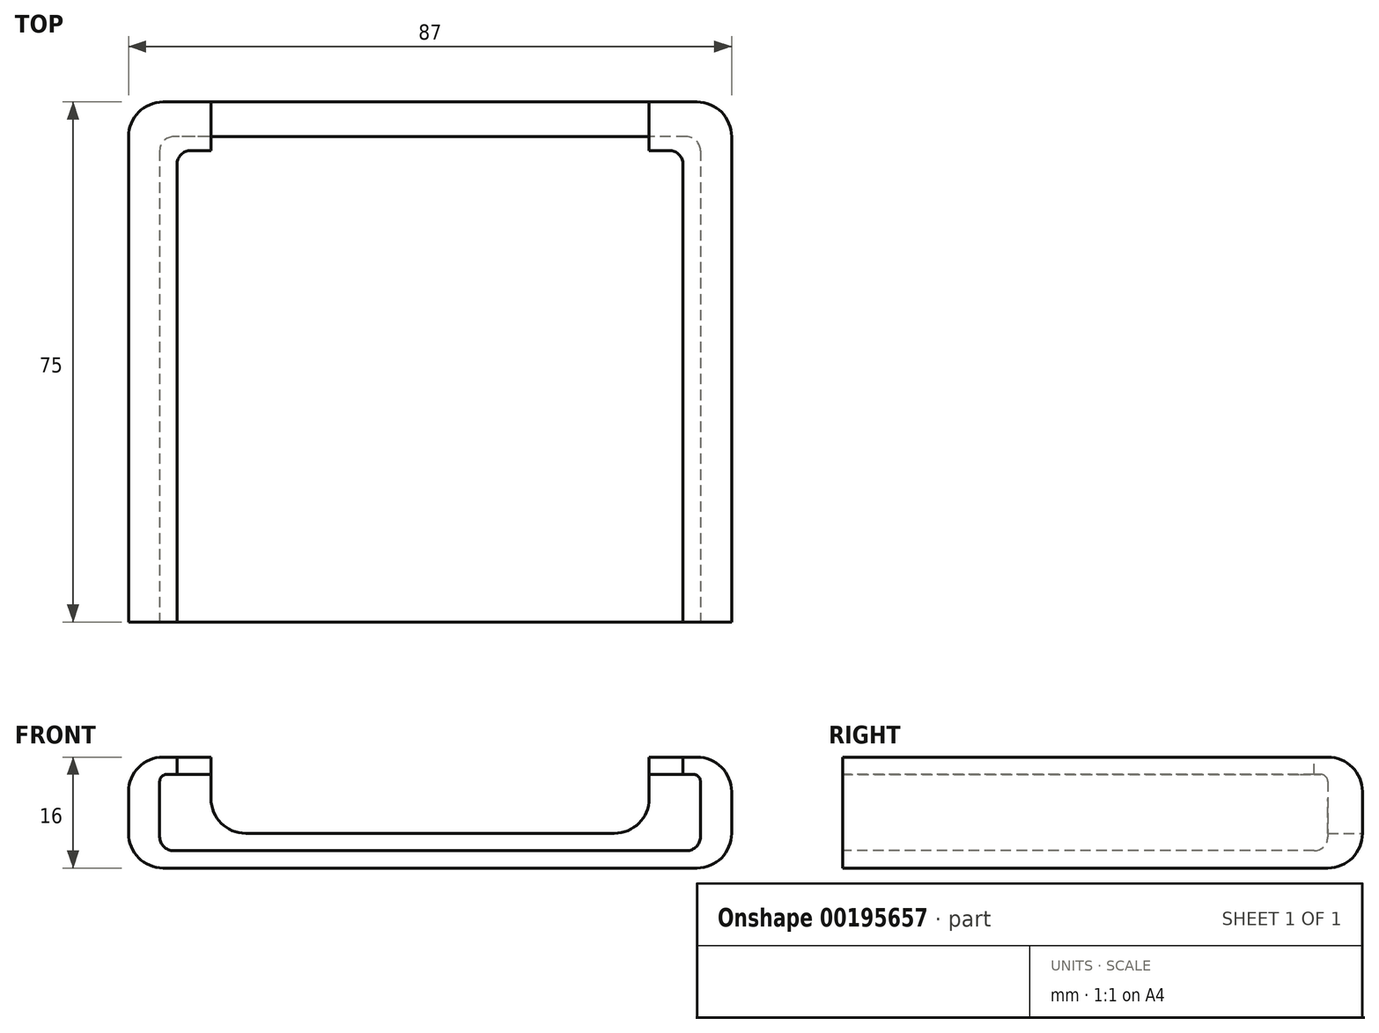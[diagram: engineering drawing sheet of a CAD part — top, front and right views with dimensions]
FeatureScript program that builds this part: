
annotation { "Feature Type Name" : "Feature", "Feature Type Description" : "" }
export const myFeature = defineFeature(function(context is Context, id is Id, definition is map)
    precondition{}
    {
        {
            var Q0;
            Q0=qCreatedBy(makeId("Front.planeOp"),FACE);
            var sketch = newSketch(context, id + "F0", { "sketchPlane" : qUnion([Q0])});
            skLineSegment(sketch, "E0.bottom", {"start": v(43.5, 8) * mm, "end": v(-43.5, 8) * mm});
            skLineSegment(sketch, "E0.top", {"start": v(43.5, -8) * mm, "end": v(-43.5, -8) * mm});
            skLineSegment(sketch, "E0.left", {"start": v(43.5, 8) * mm, "end": v(43.5, -8) * mm});
            skLineSegment(sketch, "E0.right", {"start": v(-43.5, 8) * mm, "end": v(-43.5, -8) * mm});
            skPoint(sketch, "E0.middle", {"position": v(0, 0) * mm});
            skSolve(sketch);
        }
        {
            var Q0;
            Q0=makeQuery(id+"F0.imprint","IMPRINT",FACE,{"disambiguationData":[TD([[makeQuery(id+"F0.imprint","IMPRINT",EDGE,{"derivedFrom":sQuery(id+"F0.wireOp",EDGE,"E0.bottom")}),1.0]])]});
            extrude(context, id + "F1", {"entities" : qUnion([Q0]), "depth" : 75 * mm});
        }
        {
            var Q0;
            Q0=makeQuery(id+"F1.opExtrude","SWEPT_EDGE",EDGE,{"disambiguationData":[OSD([sQuery(id+"F0.wireOp",EDGE,"E0.bottom"),sQuery(id+"F0.wireOp",EDGE,"E0.right")])]});
            var Q1;
            Q1=makeQuery(id+"F1.opExtrude","SWEPT_EDGE",EDGE,{"disambiguationData":[OSD([sQuery(id+"F0.wireOp",EDGE,"E0.bottom"),sQuery(id+"F0.wireOp",EDGE,"E0.left")])]});
            var Q2;
            Q2=makeQuery(id+"F1.opExtrude","SWEPT_EDGE",EDGE,{"disambiguationData":[OSD([sQuery(id+"F0.wireOp",EDGE,"E0.top"),sQuery(id+"F0.wireOp",EDGE,"E0.left")])]});
            var Q3;
            Q3=makeQuery(id+"F1.opExtrude","SWEPT_EDGE",EDGE,{"disambiguationData":[OSD([sQuery(id+"F0.wireOp",EDGE,"E0.top"),sQuery(id+"F0.wireOp",EDGE,"E0.right")])]});
            var Q4;
            Q4=makeQuery(id+"F1.opExtrude","CAP_EDGE",EDGE,{"disambiguationData":[OSD([sQuery(id+"F0.wireOp",EDGE,"E0.bottom")])],"isStart":true});
            var Q5;
            Q5=makeQuery(id+"F1.opExtrude","CAP_EDGE",EDGE,{"disambiguationData":[OSD([sQuery(id+"F0.wireOp",EDGE,"E0.top")])],"isStart":true});
            var Q6;
            Q6=makeQuery(id+"F1.opExtrude","CAP_EDGE",EDGE,{"disambiguationData":[OSD([sQuery(id+"F0.wireOp",EDGE,"E0.right")])],"isStart":true});
            var Q7;
            Q7=makeQuery(id+"F1.opExtrude","CAP_EDGE",EDGE,{"disambiguationData":[OSD([sQuery(id+"F0.wireOp",EDGE,"E0.left")])],"isStart":true});
            fillet(context, id + "F2", {"entities" : qUnion([Q0, Q1, Q2, Q3, Q4, Q5, Q6, Q7]), "radius" : 5 * mm, "tangentPropagation" : true, "allowEdgeOverflow" : false});
        }
        {
            var Q0;
            Q0=makeQuery(id+"F1.opExtrude","CAP_FACE",FACE,{"disambiguationData":[OSD([sQuery(id+"F0.wireOp",EDGE,"E0.bottom"),sQuery(id+"F0.wireOp",EDGE,"E0.top"),sQuery(id+"F0.wireOp",EDGE,"E0.left"),sQuery(id+"F0.wireOp",EDGE,"E0.right")])],"isStart":false});
            var sketch = newSketch(context, id + "F3", { "sketchPlane" : qUnion([Q0])});
            skLineSegment(sketch, "E1.bottom", {"start": v(39, 5.5) * mm, "end": v(-39, 5.5) * mm});
            skLineSegment(sketch, "E1.top", {"start": v(39, -5.5) * mm, "end": v(-39, -5.5) * mm});
            skLineSegment(sketch, "E1.left", {"start": v(39, 5.5) * mm, "end": v(39, -5.5) * mm});
            skLineSegment(sketch, "E1.right", {"start": v(-39, 5.5) * mm, "end": v(-39, -5.5) * mm});
            skPoint(sketch, "E1.middle", {"position": v(0, 0) * mm});
            skSolve(sketch);
        }
        {
            var Q0;
            Q0 = qSketchRegion(id + "F3", true);
            extrude(context, id + "F4", {"entities" : qUnion([Q0]), "operationType" : NewBodyOperationType.REMOVE, "oppositeDirection" : true, "depth" : 70 * mm});
        }
        {
            var Q0;
            Q0=makeQuery(id+"F1.opExtrude","SWEPT_FACE",FACE,{"disambiguationData":[OSD([sQuery(id+"F0.wireOp",EDGE,"E0.bottom")])]});
            var sketch = newSketch(context, id + "F5", { "sketchPlane" : qUnion([Q0])});
            skLineSegment(sketch, "E2.bottom", {"start": v(36.5, -7) * mm, "end": v(-36.5, -7) * mm});
            skLineSegment(sketch, "E2.top", {"start": v(36.5, -143) * mm, "end": v(-36.5, -143) * mm});
            skLineSegment(sketch, "E2.left", {"start": v(36.5, -7) * mm, "end": v(36.5, -143) * mm});
            skLineSegment(sketch, "E2.right", {"start": v(-36.5, -7) * mm, "end": v(-36.5, -143) * mm});
            skPoint(sketch, "E2.middle", {"position": v(0, -75) * mm});
            skSolve(sketch);
        }
        {
            var Q0;
            {var subQ0=sQuery(id+"F5.wireOp",EDGE,"E2.bottom");Q0=makeQuery(id+"F5.imprint","IMPRINT",FACE,{"disambiguationData":[TD([[makeQuery(id+"F5.imprint","IMPRINT",EDGE,{"derivedFrom":subQ0}),1.0]])]});}
            extrude(context, id + "F6", {"entities" : qUnion([Q0]), "operationType" : NewBodyOperationType.REMOVE, "endBound" : BoundingType.UP_TO_NEXT, "oppositeDirection" : true, "depth" : 25 * mm});
        }
        {
            var Q0;
            Q0=makeQuery(id+"F6.boolean.opBoolean","COPY",EDGE,{"derivedFrom":makeQuery(id+"F6.opExtrude","SWEPT_EDGE",EDGE,{"disambiguationData":[OSD([sQuery(id+"F5.wireOp",EDGE,"E2.bottom"),sQuery(id+"F5.wireOp",EDGE,"E2.left")])]})});
            var Q1;
            Q1=makeQuery(id+"F6.boolean.opBoolean","COPY",EDGE,{"derivedFrom":makeQuery(id+"F6.opExtrude","SWEPT_EDGE",EDGE,{"disambiguationData":[OSD([sQuery(id+"F5.wireOp",EDGE,"E2.bottom"),sQuery(id+"F5.wireOp",EDGE,"E2.right")])]})});
            var Q2;
            Q2=makeQuery(id+"F4.boolean.opBoolean","COPY",EDGE,{"derivedFrom":makeQuery(id+"F4.opExtrude","SWEPT_EDGE",EDGE,{"disambiguationData":[OSD([sQuery(id+"F3.wireOp",EDGE,"E1.top"),sQuery(id+"F3.wireOp",EDGE,"E1.left")])]})});
            var Q3;
            Q3=makeQuery(id+"F4.boolean.opBoolean","COPY",EDGE,{"derivedFrom":makeQuery(id+"F4.opExtrude","CAP_EDGE",EDGE,{"disambiguationData":[OSD([sQuery(id+"F3.wireOp",EDGE,"E1.top")])],"isStart":false})});
            var Q4;
            Q4=makeQuery(id+"F4.boolean.opBoolean","COPY",EDGE,{"derivedFrom":makeQuery(id+"F4.opExtrude","SWEPT_EDGE",EDGE,{"disambiguationData":[OSD([sQuery(id+"F3.wireOp",EDGE,"E1.top"),sQuery(id+"F3.wireOp",EDGE,"E1.right")])]})});
            var Q5;
            Q5=makeQuery(id+"F4.boolean.opBoolean","COPY",EDGE,{"derivedFrom":makeQuery(id+"F4.opExtrude","CAP_EDGE",EDGE,{"disambiguationData":[OSD([sQuery(id+"F3.wireOp",EDGE,"E1.right")])],"isStart":false})});
            var Q6;
            Q6=makeQuery(id+"F4.boolean.opBoolean","COPY",EDGE,{"derivedFrom":makeQuery(id+"F4.opExtrude","CAP_EDGE",EDGE,{"disambiguationData":[OSD([sQuery(id+"F3.wireOp",EDGE,"E1.left")])],"isStart":false})});
            fillet(context, id + "F7", {"entities" : qUnion([Q0, Q1, Q2, Q3, Q4, Q5, Q6]), "radius" : 2 * mm, "tangentPropagation" : true, "allowEdgeOverflow" : false});
        }
        {
            var Q0;
            Q0=makeQuery(id+"F1.opExtrude","CAP_FACE",FACE,{"disambiguationData":[OSD([sQuery(id+"F0.wireOp",EDGE,"E0.bottom"),sQuery(id+"F0.wireOp",EDGE,"E0.top"),sQuery(id+"F0.wireOp",EDGE,"E0.left"),sQuery(id+"F0.wireOp",EDGE,"E0.right")])],"isStart":true});
            var sketch = newSketch(context, id + "F8", { "sketchPlane" : qUnion([Q0])});
            skLineSegment(sketch, "E3.bottom", {"start": v(-26.6, -3) * mm, "end": v(26.6, -3) * mm});
            skLineSegment(sketch, "E3.top", {"start": v(-31.6, 20) * mm, "end": v(31.6, 20) * mm});
            skLineSegment(sketch, "E3.left", {"start": v(-31.6, 2) * mm, "end": v(-31.6, 20) * mm});
            skLineSegment(sketch, "E3.right", {"start": v(31.6, 2) * mm, "end": v(31.6, 20) * mm});
            skPoint(sketch, "E3.middle", {"position": v(0, 8.5) * mm});
            skPoint(sketch, "E4.visualSharp", {"position": v(-31.6, -3) * mm});
            skArc(sketch, "E4.filletArc", {"start": v(-31.6, 2) * mm, "mid": v(-30.13, -1.54) * mm, "end": v(-26.6, -3) * mm});
            skPoint(sketch, "E5.visualSharp", {"position": v(31.6, -3) * mm});
            skArc(sketch, "E5.filletArc", {"start": v(26.6, -3) * mm, "mid": v(30.13, -1.54) * mm, "end": v(31.6, 2) * mm});
            skSolve(sketch);
        }
        {
            var Q0;
            Q0=makeQuery(id+"F8.imprint","IMPRINT",FACE,{"disambiguationData":[TD([[makeQuery(id+"F8.imprint","IMPRINT",EDGE,{"derivedFrom":sQuery(id+"F8.wireOp",EDGE,"E3.bottom")}),1.0]])]});
            var Q1;
            {var subQ0=sQuery(id+"F8.wireOp",EDGE,"E3.top");Q1=makeQuery(id+"F8.imprint","IMPRINT",FACE,{"disambiguationData":[TD([[makeQuery(id+"F8.imprint","IMPRINT",EDGE,{"derivedFrom":subQ0}),-1.0]])]});}
            extrude(context, id + "F9", {"entities" : qUnion([Q0, Q1]), "operationType" : NewBodyOperationType.REMOVE, "oppositeDirection" : true, "depth" : 25 * mm});
        }
        {
            var Q0;
            Q0=makeQuery(id+"F4.boolean.opBoolean","COPY",EDGE,{"derivedFrom":makeQuery(id+"F4.opExtrude","SWEPT_EDGE",EDGE,{"disambiguationData":[OSD([sQuery(id+"F3.wireOp",EDGE,"E1.bottom"),sQuery(id+"F3.wireOp",EDGE,"E1.left")])]})});
            var Q1;
            Q1=makeQuery(id+"F4.boolean.opBoolean","COPY",EDGE,{"derivedFrom":makeQuery(id+"F4.opExtrude","SWEPT_EDGE",EDGE,{"disambiguationData":[OSD([sQuery(id+"F3.wireOp",EDGE,"E1.bottom"),sQuery(id+"F3.wireOp",EDGE,"E1.right")])]})});
            fillet(context, id + "F10", {"entities" : qUnion([Q0, Q1]), "radius" : 1 * mm, "tangentPropagation" : true, "allowEdgeOverflow" : false});
        }
    });
